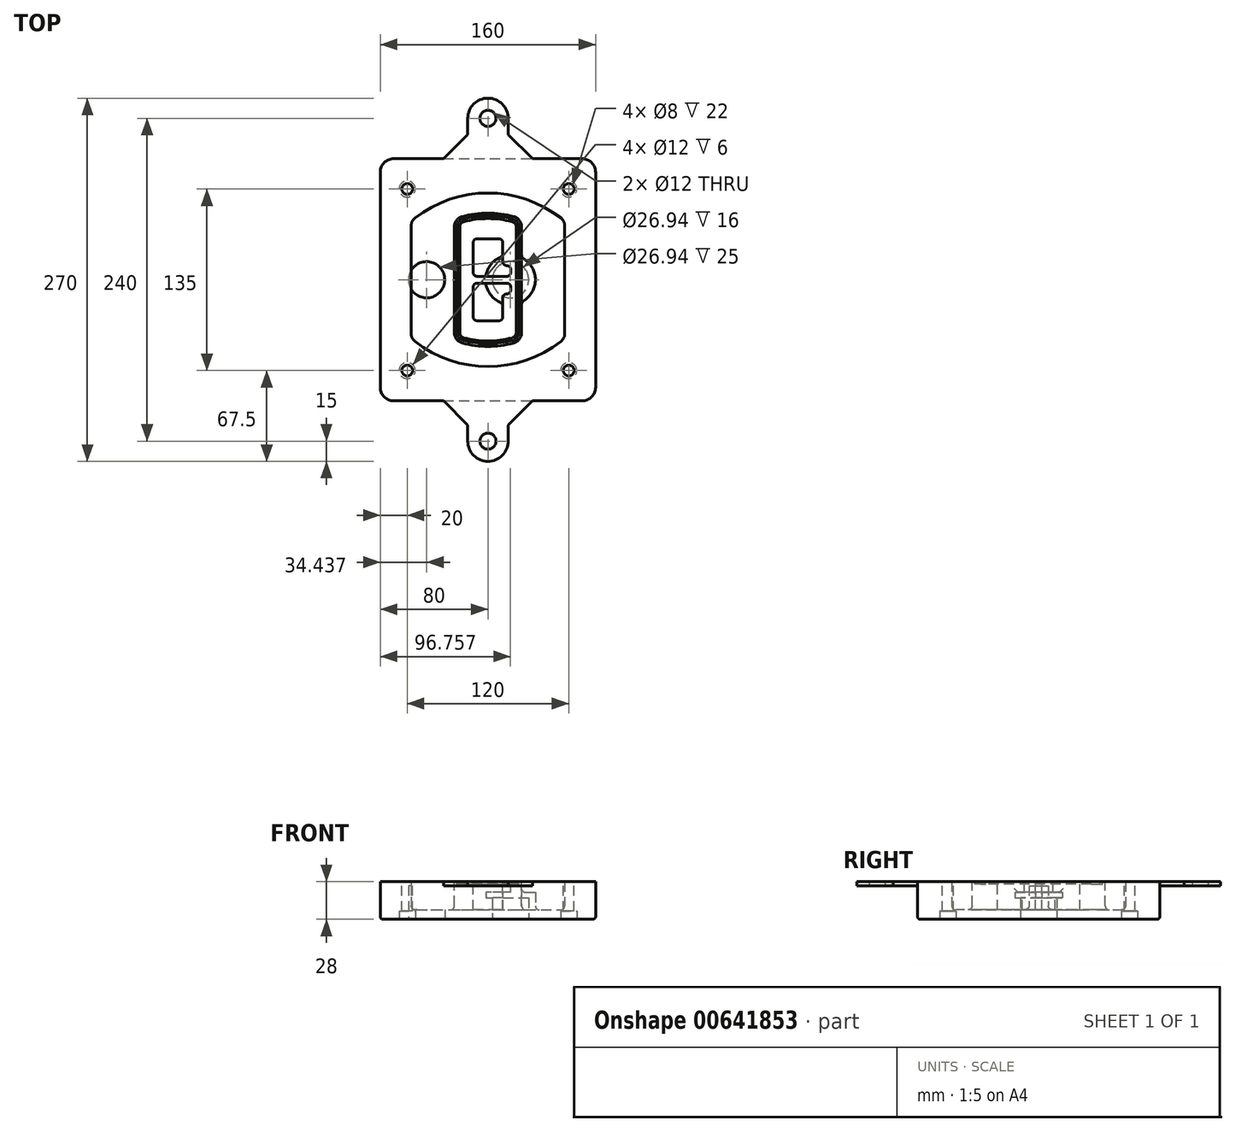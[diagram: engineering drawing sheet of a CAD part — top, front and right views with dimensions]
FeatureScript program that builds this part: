
annotation { "Feature Type Name" : "Feature", "Feature Type Description" : "" }
export const myFeature = defineFeature(function(context is Context, id is Id, definition is map)
    precondition{}
    {
        {
            var Q0;
            Q0=qCreatedBy(makeId("Top.planeOp"),FACE);
            var sketch = newSketch(context, id + "F0", { "sketchPlane" : qUnion([Q0])});
            skPoint(sketch, "E0.rect.middle", {"position": v(0, 0) * mm});
            skLineSegment(sketch, "E1.bottom", {"start": v(-70, -90) * mm, "end": v(70, -90) * mm});
            skLineSegment(sketch, "E1.top", {"start": v(-70, 90) * mm, "end": v(70, 90) * mm});
            skLineSegment(sketch, "E1.left", {"start": v(-80, -80) * mm, "end": v(-80, 80) * mm});
            skLineSegment(sketch, "E1.right", {"start": v(80, -80) * mm, "end": v(80, 80) * mm});
            skLineSegment(sketch, "E2", {"start": v(-80, 90) * mm, "end": v(80, -90) * mm, "construction": true});
            skLineSegment(sketch, "E3", {"start": v(80, 90) * mm, "end": v(-80, -90) * mm, "construction": true});
            skCircle(sketch, "E4", {"center": v(-60, 67.5) * mm, "radius": 4 * mm});
            skCircle(sketch, "E5", {"center": v(60, 67.5) * mm, "radius": 4 * mm});
            skCircle(sketch, "E6", {"center": v(60, -67.5) * mm, "radius": 4 * mm});
            skCircle(sketch, "E7", {"center": v(-60, -67.5) * mm, "radius": 4 * mm});
            skLineSegment(sketch, "E8", {"start": v(-60, 67.5) * mm, "end": v(60, 67.5) * mm, "construction": true});
            skLineSegment(sketch, "E9", {"start": v(60, 67.5) * mm, "end": v(60, -67.5) * mm, "construction": true});
            skLineSegment(sketch, "E10", {"start": v(60, -67.5) * mm, "end": v(-60, -67.5) * mm, "construction": true});
            skLineSegment(sketch, "E11", {"start": v(-60, -67.5) * mm, "end": v(-60, 67.5) * mm, "construction": true});
            skLineSegment(sketch, "E12", {"start": v(-60, 40.3) * mm, "end": v(-60, -40.3) * mm});
            skLineSegment(sketch, "E13", {"start": v(60, 40.3) * mm, "end": v(60, -40.3) * mm});
            skArc(sketch, "E14", {"start": v(56.15, 48.18) * mm, "mid": v(0, 67.5) * mm, "end": v(-56.15, 48.18) * mm});
            skArc(sketch, "E15", {"start": v(-56.15, -48.18) * mm, "mid": v(0, -67.5) * mm, "end": v(56.15, -48.18) * mm});
            skLineSegment(sketch, "E16", {"start": v(-60, 0) * mm, "end": v(60, 0) * mm, "construction": true});
            skPoint(sketch, "E17.visualSharp", {"position": v(-60, -45) * mm});
            skArc(sketch, "E17.filletArc", {"start": v(-60, -40.3) * mm, "mid": v(-58.99, -44.68) * mm, "end": v(-56.15, -48.18) * mm});
            skPoint(sketch, "E18.visualSharp", {"position": v(-60, 45) * mm});
            skArc(sketch, "E18.filletArc", {"start": v(-56.15, 48.18) * mm, "mid": v(-58.99, 44.68) * mm, "end": v(-60, 40.3) * mm});
            skPoint(sketch, "E19.visualSharp", {"position": v(60, 45) * mm});
            skArc(sketch, "E19.filletArc", {"start": v(60, 40.3) * mm, "mid": v(58.99, 44.68) * mm, "end": v(56.15, 48.18) * mm});
            skPoint(sketch, "E20.visualSharp", {"position": v(60, -45) * mm});
            skArc(sketch, "E20.filletArc", {"start": v(56.15, -48.18) * mm, "mid": v(58.99, -44.68) * mm, "end": v(60, -40.3) * mm});
            skPoint(sketch, "E21.visualSharp", {"position": v(-80, 90) * mm});
            skArc(sketch, "E21.filletArc", {"start": v(-70, 90) * mm, "mid": v(-77.07, 87.07) * mm, "end": v(-80, 80) * mm});
            skPoint(sketch, "E22.visualSharp", {"position": v(80, 90) * mm});
            skArc(sketch, "E22.filletArc", {"start": v(80, 80) * mm, "mid": v(77.07, 87.07) * mm, "end": v(70, 90) * mm});
            skPoint(sketch, "E23.visualSharp", {"position": v(80, -90) * mm});
            skArc(sketch, "E23.filletArc", {"start": v(70, -90) * mm, "mid": v(77.07, -87.07) * mm, "end": v(80, -80) * mm});
            skPoint(sketch, "E24.visualSharp", {"position": v(-80, -90) * mm});
            skArc(sketch, "E24.filletArc", {"start": v(-80, -80) * mm, "mid": v(-77.07, -87.07) * mm, "end": v(-70, -90) * mm});
            skArc(sketch, "E25.0", {"start": v(57, 40.3) * mm, "mid": v(56.3, 43.36) * mm, "end": v(54.3, 45.81) * mm});
            skLineSegment(sketch, "E25.1", {"start": v(57, 40.3) * mm, "end": v(57, -40.3) * mm});
            skArc(sketch, "E25.2", {"start": v(54.3, -45.81) * mm, "mid": v(56.3, -43.36) * mm, "end": v(57, -40.3) * mm});
            skArc(sketch, "E25.3", {"start": v(-54.3, -45.81) * mm, "mid": v(0, -64.5) * mm, "end": v(54.3, -45.81) * mm});
            skArc(sketch, "E25.4", {"start": v(-57, -40.3) * mm, "mid": v(-56.3, -43.36) * mm, "end": v(-54.3, -45.81) * mm});
            skArc(sketch, "E25.5", {"start": v(54.3, 45.81) * mm, "mid": v(0, 64.5) * mm, "end": v(-54.3, 45.81) * mm});
            skLineSegment(sketch, "E25.6", {"start": v(-57, 40.3) * mm, "end": v(-57, -40.3) * mm});
            skArc(sketch, "E25.7", {"start": v(-54.3, 45.81) * mm, "mid": v(-56.3, 43.36) * mm, "end": v(-57, 40.3) * mm});
            skArc(sketch, "E26.0", {"start": v(-58.62, 51.33) * mm, "mid": v(-62.58, 46.43) * mm, "end": v(-64, 40.3) * mm});
            skArc(sketch, "E26.1", {"start": v(58.62, 51.33) * mm, "mid": v(0, 71.5) * mm, "end": v(-58.62, 51.33) * mm});
            skArc(sketch, "E26.2", {"start": v(64, 40.3) * mm, "mid": v(62.58, 46.43) * mm, "end": v(58.62, 51.33) * mm});
            skLineSegment(sketch, "E26.3", {"start": v(64, 40.3) * mm, "end": v(64, -40.3) * mm});
            skArc(sketch, "E26.4", {"start": v(58.62, -51.33) * mm, "mid": v(62.58, -46.43) * mm, "end": v(64, -40.3) * mm});
            skLineSegment(sketch, "E26.5", {"start": v(-64, 40.3) * mm, "end": v(-64, -40.3) * mm});
            skArc(sketch, "E26.6", {"start": v(-58.62, -51.33) * mm, "mid": v(0, -71.5) * mm, "end": v(58.62, -51.33) * mm});
            skArc(sketch, "E26.7", {"start": v(-64, -40.3) * mm, "mid": v(-62.58, -46.43) * mm, "end": v(-58.62, -51.33) * mm});
            skSolve(sketch);
        }
        {
            var Q0;
            Q0=makeQuery(id+"F0.imprint","IMPRINT",FACE,{"disambiguationData":[TD([[makeQuery(id+"F0.imprint","IMPRINT",EDGE,{"derivedFrom":sQuery(id+"F0.wireOp",EDGE,"E1.bottom")}),1.0]])]});
            var Q1;
            Q1=makeQuery(id+"F0.imprint","IMPRINT",FACE,{"disambiguationData":[TD([[makeQuery(id+"F0.imprint","IMPRINT",EDGE,{"derivedFrom":sQuery(id+"F0.wireOp",EDGE,"E12")}),1.0]])]});
            var Q2;
            Q2=makeQuery(id+"F0.imprint","IMPRINT",FACE,{"disambiguationData":[TD([[makeQuery(id+"F0.imprint","IMPRINT",EDGE,{"derivedFrom":sQuery(id+"F0.wireOp",EDGE,"E25.0")}),1.0]])]});
            var Q3;
            Q3=makeQuery(id+"F0.imprint","IMPRINT",FACE,{"disambiguationData":[TD([[makeQuery(id+"F0.imprint","IMPRINT",EDGE,{"derivedFrom":sQuery(id+"F0.wireOp",EDGE,"E12")}),-1.0]])]});
            extrude(context, id + "F1", {"entities" : qUnion([Q0, Q1, Q2, Q3]), "oppositeDirection" : true, "depth" : 25 * mm});
        }
        {
            var Q0;
            Q0=makeQuery(id+"F0.imprint","IMPRINT",FACE,{"disambiguationData":[TD([[makeQuery(id+"F0.imprint","IMPRINT",EDGE,{"derivedFrom":sQuery(id+"F0.wireOp",EDGE,"E12")}),1.0]])]});
            extrude(context, id + "F2", {"entities" : qUnion([Q0]), "operationType" : NewBodyOperationType.ADD, "depth" : 3 * mm});
        }
        {
            var Q0;
            Q0=makeQuery(id+"F0.imprint","IMPRINT",FACE,{"disambiguationData":[TD([[makeQuery(id+"F0.imprint","IMPRINT",EDGE,{"derivedFrom":sQuery(id+"F0.wireOp",EDGE,"E25.0")}),1.0]])]});
            extrude(context, id + "F3", {"entities" : qUnion([Q0]), "operationType" : NewBodyOperationType.REMOVE, "oppositeDirection" : true, "depth" : 18 * mm});
        }
        {
            var Q0;
            Q0=makeQuery(id+"F2.opExtrude","CAP_FACE",FACE,{"disambiguationData":[OSD([sQuery(id+"F0.wireOp",EDGE,"E12"),sQuery(id+"F0.wireOp",EDGE,"E13"),sQuery(id+"F0.wireOp",EDGE,"E14"),sQuery(id+"F0.wireOp",EDGE,"E15"),sQuery(id+"F0.wireOp",EDGE,"E17.filletArc"),sQuery(id+"F0.wireOp",EDGE,"E18.filletArc"),sQuery(id+"F0.wireOp",EDGE,"E19.filletArc"),sQuery(id+"F0.wireOp",EDGE,"E20.filletArc"),sQuery(id+"F0.wireOp",EDGE,"E25.0"),sQuery(id+"F0.wireOp",EDGE,"E25.1"),sQuery(id+"F0.wireOp",EDGE,"E25.2"),sQuery(id+"F0.wireOp",EDGE,"E25.3"),sQuery(id+"F0.wireOp",EDGE,"E25.4"),sQuery(id+"F0.wireOp",EDGE,"E25.5"),sQuery(id+"F0.wireOp",EDGE,"E25.6"),sQuery(id+"F0.wireOp",EDGE,"E25.7")])],"isStart":false});
            var sketch = newSketch(context, id + "F4", { "sketchPlane" : qUnion([Q0])});
            skArc(sketch, "E27.0", {"start": v(-19.08, -46.97) * mm, "mid": v(0, -49.5) * mm, "end": v(19.08, -46.97) * mm});
            skArc(sketch, "E28.0", {"start": v(19.08, 46.97) * mm, "mid": v(0, 49.5) * mm, "end": v(-19.08, 46.97) * mm});
            skLineSegment(sketch, "E29", {"start": v(-25, 39.25) * mm, "end": v(-25, -39.25) * mm});
            skLineSegment(sketch, "E30", {"start": v(25, 39.25) * mm, "end": v(25, -39.25) * mm});
            skLineSegment(sketch, "E31", {"start": v(-25, 45.1) * mm, "end": v(25, 45.1) * mm, "construction": true});
            skLineSegment(sketch, "E32", {"start": v(-25, -45.1) * mm, "end": v(25, -45.1) * mm, "construction": true});
            skPoint(sketch, "E33.visualSharp", {"position": v(-25, 45.1) * mm});
            skArc(sketch, "E33.filletArc", {"start": v(-19.08, 46.97) * mm, "mid": v(-23.35, 44.11) * mm, "end": v(-25, 39.25) * mm});
            skPoint(sketch, "E34.visualSharp", {"position": v(25, 45.1) * mm});
            skArc(sketch, "E34.filletArc", {"start": v(25, 39.25) * mm, "mid": v(23.35, 44.11) * mm, "end": v(19.08, 46.97) * mm});
            skPoint(sketch, "E35.visualSharp", {"position": v(25, -45.1) * mm});
            skArc(sketch, "E35.filletArc", {"start": v(19.08, -46.97) * mm, "mid": v(23.35, -44.11) * mm, "end": v(25, -39.25) * mm});
            skPoint(sketch, "E36.visualSharp", {"position": v(-25, -45.1) * mm});
            skArc(sketch, "E36.filletArc", {"start": v(-25, -39.25) * mm, "mid": v(-23.35, -44.11) * mm, "end": v(-19.08, -46.97) * mm});
            skArc(sketch, "E37.0", {"start": v(54.3, 45.81) * mm, "mid": v(0, 64.5) * mm, "end": v(-54.3, 45.81) * mm});
            skArc(sketch, "E37.1", {"start": v(-54.3, 45.81) * mm, "mid": v(-56.3, 43.36) * mm, "end": v(-57, 40.3) * mm});
            skLineSegment(sketch, "E37.2", {"start": v(-57, 40.3) * mm, "end": v(-57, -40.3) * mm});
            skArc(sketch, "E37.3", {"start": v(-57, -40.3) * mm, "mid": v(-56.3, -43.36) * mm, "end": v(-54.3, -45.81) * mm});
            skArc(sketch, "E37.4", {"start": v(-54.3, -45.81) * mm, "mid": v(0, -64.5) * mm, "end": v(54.3, -45.81) * mm});
            skArc(sketch, "E37.5", {"start": v(54.3, -45.81) * mm, "mid": v(56.3, -43.36) * mm, "end": v(57, -40.3) * mm});
            skLineSegment(sketch, "E37.6", {"start": v(57, 40.3) * mm, "end": v(57, -40.3) * mm});
            skArc(sketch, "E37.7", {"start": v(57, 40.3) * mm, "mid": v(56.3, 43.36) * mm, "end": v(54.3, 45.81) * mm});
            skLineSegment(sketch, "E38.0", {"start": v(23, 39.25) * mm, "end": v(23, -39.25) * mm});
            skArc(sketch, "E38.1", {"start": v(18.56, -45.04) * mm, "mid": v(21.76, -42.9) * mm, "end": v(23, -39.25) * mm});
            skArc(sketch, "E38.2", {"start": v(-18.56, -45.04) * mm, "mid": v(0, -47.5) * mm, "end": v(18.56, -45.04) * mm});
            skArc(sketch, "E38.3", {"start": v(-23, -39.25) * mm, "mid": v(-21.76, -42.9) * mm, "end": v(-18.56, -45.04) * mm});
            skLineSegment(sketch, "E38.4", {"start": v(-23, 39.25) * mm, "end": v(-23, -39.25) * mm});
            skArc(sketch, "E38.5", {"start": v(23, 39.25) * mm, "mid": v(21.76, 42.9) * mm, "end": v(18.56, 45.04) * mm});
            skArc(sketch, "E38.6", {"start": v(-18.56, 45.04) * mm, "mid": v(-21.76, 42.9) * mm, "end": v(-23, 39.25) * mm});
            skArc(sketch, "E38.7", {"start": v(18.56, 45.04) * mm, "mid": v(0, 47.5) * mm, "end": v(-18.56, 45.04) * mm});
            skArc(sketch, "E39.0", {"start": v(21, 39.25) * mm, "mid": v(20.18, 41.68) * mm, "end": v(18.04, 43.1) * mm});
            skLineSegment(sketch, "E39.1", {"start": v(21, 39.25) * mm, "end": v(21, -39.25) * mm});
            skArc(sketch, "E39.2", {"start": v(18.04, -43.1) * mm, "mid": v(20.18, -41.68) * mm, "end": v(21, -39.25) * mm});
            skArc(sketch, "E39.3", {"start": v(-18.04, -43.1) * mm, "mid": v(0, -45.5) * mm, "end": v(18.04, -43.1) * mm});
            skArc(sketch, "E39.4", {"start": v(-21, -39.25) * mm, "mid": v(-20.18, -41.68) * mm, "end": v(-18.04, -43.1) * mm});
            skArc(sketch, "E39.5", {"start": v(18.04, 43.1) * mm, "mid": v(0, 45.5) * mm, "end": v(-18.04, 43.1) * mm});
            skLineSegment(sketch, "E39.6", {"start": v(-21, 39.25) * mm, "end": v(-21, -39.25) * mm});
            skArc(sketch, "E39.7", {"start": v(-18.04, 43.1) * mm, "mid": v(-20.18, 41.68) * mm, "end": v(-21, 39.25) * mm});
            skLineSegment(sketch, "E40", {"start": v(-25, 0) * mm, "end": v(25, 0) * mm, "construction": true});
            skLineSegment(sketch, "E41", {"start": v(-11, 5.5) * mm, "end": v(-11, 27.5) * mm});
            skLineSegment(sketch, "E42", {"start": v(-8, 30.5) * mm, "end": v(8, 30.5) * mm});
            skLineSegment(sketch, "E43", {"start": v(11, 27.5) * mm, "end": v(11, 13.5) * mm});
            skLineSegment(sketch, "E44", {"start": v(14, 10.5) * mm, "end": v(14, 10.5) * mm});
            skLineSegment(sketch, "E45", {"start": v(17, 7.5) * mm, "end": v(17, 5.5) * mm});
            skLineSegment(sketch, "E46", {"start": v(14, 2.5) * mm, "end": v(-8, 2.5) * mm});
            skPoint(sketch, "E47.visualSharp", {"position": v(-11, 30.5) * mm});
            skArc(sketch, "E47.filletArc", {"start": v(-8, 30.5) * mm, "mid": v(-10.12, 29.62) * mm, "end": v(-11, 27.5) * mm});
            skPoint(sketch, "E48.visualSharp", {"position": v(11, 30.5) * mm});
            skArc(sketch, "E48.filletArc", {"start": v(11, 27.5) * mm, "mid": v(10.12, 29.62) * mm, "end": v(8, 30.5) * mm});
            skPoint(sketch, "E49.visualSharp", {"position": v(11, 10.5) * mm});
            skArc(sketch, "E49.filletArc", {"start": v(11, 13.5) * mm, "mid": v(11.88, 11.38) * mm, "end": v(14, 10.5) * mm});
            skPoint(sketch, "E50.visualSharp", {"position": v(17, 10.5) * mm});
            skArc(sketch, "E50.filletArc", {"start": v(17, 7.5) * mm, "mid": v(16.12, 9.62) * mm, "end": v(14, 10.5) * mm});
            skPoint(sketch, "E51.visualSharp", {"position": v(17, 2.5) * mm});
            skArc(sketch, "E51.filletArc", {"start": v(14, 2.5) * mm, "mid": v(16.12, 3.38) * mm, "end": v(17, 5.5) * mm});
            skPoint(sketch, "E52.visualSharp", {"position": v(-11, 2.5) * mm});
            skArc(sketch, "E52.filletArc", {"start": v(-11, 5.5) * mm, "mid": v(-10.12, 3.38) * mm, "end": v(-8, 2.5) * mm});
            skLineSegment(sketch, "E53.0.MirrorCS", {"start": v(14, -2.5) * mm, "end": v(-8, -2.5) * mm});
            skArc(sketch, "E54.0.MirrorCS", {"start": v(-11, -5.5) * mm, "mid": v(-10.12, -3.38) * mm, "end": v(-8, -2.5) * mm});
            skLineSegment(sketch, "E55.0.MirrorCS", {"start": v(-11, -5.5) * mm, "end": v(-11, -27.5) * mm});
            skArc(sketch, "E56.0.MirrorCS", {"start": v(-8, -30.5) * mm, "mid": v(-10.12, -29.62) * mm, "end": v(-11, -27.5) * mm});
            skLineSegment(sketch, "E57.0.MirrorCS", {"start": v(-8, -30.5) * mm, "end": v(8, -30.5) * mm});
            skArc(sketch, "E58.0.MirrorCS", {"start": v(11, -27.5) * mm, "mid": v(10.12, -29.62) * mm, "end": v(8, -30.5) * mm});
            skLineSegment(sketch, "E59.0.MirrorCS", {"start": v(11, -27.5) * mm, "end": v(11, -13.5) * mm});
            skArc(sketch, "E60.0.MirrorCS", {"start": v(11, -13.5) * mm, "mid": v(11.88, -11.38) * mm, "end": v(14, -10.5) * mm});
            skArc(sketch, "E61.0.MirrorCS", {"start": v(17, -7.5) * mm, "mid": v(16.12, -9.62) * mm, "end": v(14, -10.5) * mm});
            skLineSegment(sketch, "E62.0.MirrorCS", {"start": v(17, -7.5) * mm, "end": v(17, -5.5) * mm});
            skArc(sketch, "E63.0.MirrorCS", {"start": v(14, -2.5) * mm, "mid": v(16.12, -3.38) * mm, "end": v(17, -5.5) * mm});
            skSolve(sketch);
        }
        {
            var Q0;
            Q0=makeQuery(id+"F4.imprint","IMPRINT",FACE,{"disambiguationData":[TD([[makeQuery(id+"F4.imprint","IMPRINT",EDGE,{"derivedFrom":sQuery(id+"F4.wireOp",EDGE,"E27.0")}),1.0]])]});
            var Q1;
            Q1=makeQuery(id+"F4.imprint","IMPRINT",FACE,{"disambiguationData":[TD([[makeQuery(id+"F4.imprint","IMPRINT",EDGE,{"derivedFrom":sQuery(id+"F4.wireOp",EDGE,"E38.0")}),-1.0]])]});
            var Q2;
            Q2=makeQuery(id+"F4.imprint","IMPRINT",FACE,{"disambiguationData":[TD([[makeQuery(id+"F4.imprint","IMPRINT",EDGE,{"derivedFrom":sQuery(id+"F4.wireOp",EDGE,"E39.0")}),1.0]])]});
            extrude(context, id + "F5", {"entities" : qUnion([Q0, Q1, Q2]), "operationType" : NewBodyOperationType.ADD, "endBound" : BoundingType.UP_TO_NEXT, "oppositeDirection" : true, "depth" : 25 * mm});
        }
        {
            var Q0;
            Q0=makeQuery(id+"F4.imprint","IMPRINT",FACE,{"disambiguationData":[TD([[makeQuery(id+"F4.imprint","IMPRINT",EDGE,{"derivedFrom":sQuery(id+"F4.wireOp",EDGE,"E38.0")}),-1.0]])]});
            extrude(context, id + "F6", {"entities" : qUnion([Q0]), "operationType" : NewBodyOperationType.REMOVE, "oppositeDirection" : true, "depth" : 2 * mm});
        }
        {
            var Q0;
            Q0=makeQuery(id+"F1.opExtrude","CAP_FACE",FACE,{"disambiguationData":[OSD([sQuery(id+"F0.wireOp",EDGE,"E1.bottom"),sQuery(id+"F0.wireOp",EDGE,"E1.top"),sQuery(id+"F0.wireOp",EDGE,"E1.left"),sQuery(id+"F0.wireOp",EDGE,"E1.right"),sQuery(id+"F0.wireOp",EDGE,"E4"),sQuery(id+"F0.wireOp",EDGE,"E5"),sQuery(id+"F0.wireOp",EDGE,"E6"),sQuery(id+"F0.wireOp",EDGE,"E7"),sQuery(id+"F0.wireOp",EDGE,"E21.filletArc"),sQuery(id+"F0.wireOp",EDGE,"E22.filletArc"),sQuery(id+"F0.wireOp",EDGE,"E23.filletArc"),sQuery(id+"F0.wireOp",EDGE,"E24.filletArc")])],"isStart":false});
            var sketch = newSketch(context, id + "F7", { "sketchPlane" : qUnion([Q0])});
            skCircle(sketch, "E64", {"center": v(16.76, 0) * mm, "radius": 13.47 * mm});
            skCircle(sketch, "E65", {"center": v(-45.56, 0) * mm, "radius": 13.47 * mm});
            skLineSegment(sketch, "E66", {"start": v(80, 0) * mm, "end": v(-80, 0) * mm});
            skCircle(sketch, "E67", {"center": v(16.76, 0) * mm, "radius": 18.47 * mm});
            skCircle(sketch, "E68", {"center": v(60, -67.5) * mm, "radius": 6 * mm});
            skCircle(sketch, "E69", {"center": v(-60, -67.5) * mm, "radius": 6 * mm});
            skCircle(sketch, "E70", {"center": v(-60, 67.5) * mm, "radius": 6 * mm});
            skCircle(sketch, "E71", {"center": v(60, 67.5) * mm, "radius": 6 * mm});
            skSolve(sketch);
        }
        {
            var Q0;
            {var subQ1=sQuery(id+"F7.wireOp",EDGE,"E66");var subQ4=sQuery(id+"F7.wireOp",EDGE,"E64");var subQ6=makeQuery(id+"F7.imprint","INTERSECT",VERTEX,{"disambiguationData":[OD(0.0)],"derivedFrom":[subQ4,subQ1]});Q0=makeQuery(id+"F7.imprint","IMPRINT",FACE,{"disambiguationData":[TD([[makeQuery(id+"F7.imprint","IMPRINT",EDGE,{"disambiguationData":[TD([[subQ6,-1.0]])],"derivedFrom":subQ4}),-1.0]])]});}
            var Q1;
            {var subQ0=sQuery(id+"F7.wireOp",EDGE,"E66");var subQ1=sQuery(id+"F7.wireOp",EDGE,"E64");var subQ3=makeQuery(id+"F7.imprint","INTERSECT",VERTEX,{"disambiguationData":[OD(0.0)],"derivedFrom":[subQ1,subQ0]});Q1=makeQuery(id+"F7.imprint","IMPRINT",FACE,{"disambiguationData":[TD([[makeQuery(id+"F7.imprint","IMPRINT",EDGE,{"disambiguationData":[TD([[subQ3,-1.0]])],"derivedFrom":subQ1}),1.0]])]});}
            var Q2;
            {var subQ0=sQuery(id+"F7.wireOp",EDGE,"E66");var subQ1=sQuery(id+"F7.wireOp",EDGE,"E64");var subQ3=makeQuery(id+"F7.imprint","INTERSECT",VERTEX,{"disambiguationData":[OD(0.0)],"derivedFrom":[subQ1,subQ0]});Q2=makeQuery(id+"F7.imprint","IMPRINT",FACE,{"disambiguationData":[TD([[makeQuery(id+"F7.imprint","IMPRINT",EDGE,{"disambiguationData":[TD([[subQ3,1.0]])],"derivedFrom":subQ1}),1.0]])]});}
            var Q3;
            {var subQ1=sQuery(id+"F7.wireOp",EDGE,"E66");var subQ4=sQuery(id+"F7.wireOp",EDGE,"E64");var subQ6=makeQuery(id+"F7.imprint","INTERSECT",VERTEX,{"disambiguationData":[OD(0.0)],"derivedFrom":[subQ4,subQ1]});Q3=makeQuery(id+"F7.imprint","IMPRINT",FACE,{"disambiguationData":[TD([[makeQuery(id+"F7.imprint","IMPRINT",EDGE,{"disambiguationData":[TD([[subQ6,1.0]])],"derivedFrom":subQ4}),-1.0]])]});}
            extrude(context, id + "F8", {"entities" : qUnion([Q0, Q1, Q2, Q3]), "operationType" : NewBodyOperationType.ADD, "oppositeDirection" : true, "depth" : 20 * mm});
        }
        {
            var Q0;
            {var subQ0=sQuery(id+"F7.wireOp",EDGE,"E66");var subQ1=sQuery(id+"F7.wireOp",EDGE,"E64");var subQ3=makeQuery(id+"F7.imprint","INTERSECT",VERTEX,{"disambiguationData":[OD(0.0)],"derivedFrom":[subQ1,subQ0]});Q0=makeQuery(id+"F7.imprint","IMPRINT",FACE,{"disambiguationData":[TD([[makeQuery(id+"F7.imprint","IMPRINT",EDGE,{"disambiguationData":[TD([[subQ3,-1.0]])],"derivedFrom":subQ1}),1.0]])]});}
            var Q1;
            {var subQ0=sQuery(id+"F7.wireOp",EDGE,"E66");var subQ1=sQuery(id+"F7.wireOp",EDGE,"E64");var subQ3=makeQuery(id+"F7.imprint","INTERSECT",VERTEX,{"disambiguationData":[OD(0.0)],"derivedFrom":[subQ1,subQ0]});Q1=makeQuery(id+"F7.imprint","IMPRINT",FACE,{"disambiguationData":[TD([[makeQuery(id+"F7.imprint","IMPRINT",EDGE,{"disambiguationData":[TD([[subQ3,1.0]])],"derivedFrom":subQ1}),1.0]])]});}
            extrude(context, id + "F9", {"entities" : qUnion([Q0, Q1]), "operationType" : NewBodyOperationType.REMOVE, "oppositeDirection" : true, "depth" : 16 * mm});
        }
        {
            var Q0;
            {var subQ0=sQuery(id+"F7.wireOp",EDGE,"E66");var subQ1=sQuery(id+"F7.wireOp",EDGE,"E65");var subQ3=makeQuery(id+"F7.imprint","INTERSECT",VERTEX,{"disambiguationData":[OD(0.0)],"derivedFrom":[subQ1,subQ0]});Q0=makeQuery(id+"F7.imprint","IMPRINT",FACE,{"disambiguationData":[TD([[makeQuery(id+"F7.imprint","IMPRINT",EDGE,{"disambiguationData":[TD([[subQ3,-1.0]])],"derivedFrom":subQ1}),1.0]])]});}
            var Q1;
            {var subQ0=sQuery(id+"F7.wireOp",EDGE,"E66");var subQ1=sQuery(id+"F7.wireOp",EDGE,"E65");var subQ3=makeQuery(id+"F7.imprint","INTERSECT",VERTEX,{"disambiguationData":[OD(0.0)],"derivedFrom":[subQ1,subQ0]});Q1=makeQuery(id+"F7.imprint","IMPRINT",FACE,{"disambiguationData":[TD([[makeQuery(id+"F7.imprint","IMPRINT",EDGE,{"disambiguationData":[TD([[subQ3,1.0]])],"derivedFrom":subQ1}),1.0]])]});}
            extrude(context, id + "F10", {"entities" : qUnion([Q0, Q1]), "operationType" : NewBodyOperationType.REMOVE, "oppositeDirection" : true, "depth" : 25 * mm});
        }
        {
            var Q0;
            Q0=makeQuery(id+"F7.imprint","IMPRINT",FACE,{"disambiguationData":[TD([[makeQuery(id+"F7.imprint","IMPRINT",EDGE,{"derivedFrom":sQuery(id+"F7.wireOp",EDGE,"E68")}),1.0]])]});
            var Q1;
            Q1=makeQuery(id+"F7.imprint","IMPRINT",FACE,{"disambiguationData":[TD([[makeQuery(id+"F7.imprint","IMPRINT",EDGE,{"derivedFrom":makeQuery(id+"F1.opExtrude","CAP_EDGE",EDGE,{"disambiguationData":[OSD([sQuery(id+"F0.wireOp",EDGE,"E5")])],"isStart":false})}),-1.0]])]});
            var Q2;
            Q2=makeQuery(id+"F7.imprint","IMPRINT",FACE,{"disambiguationData":[TD([[makeQuery(id+"F7.imprint","IMPRINT",EDGE,{"derivedFrom":sQuery(id+"F7.wireOp",EDGE,"E69")}),1.0]])]});
            var Q3;
            Q3=makeQuery(id+"F7.imprint","IMPRINT",FACE,{"disambiguationData":[TD([[makeQuery(id+"F7.imprint","IMPRINT",EDGE,{"derivedFrom":makeQuery(id+"F1.opExtrude","CAP_EDGE",EDGE,{"disambiguationData":[OSD([sQuery(id+"F0.wireOp",EDGE,"E4")])],"isStart":false})}),-1.0]])]});
            var Q4;
            Q4=makeQuery(id+"F7.imprint","IMPRINT",FACE,{"disambiguationData":[TD([[makeQuery(id+"F7.imprint","IMPRINT",EDGE,{"derivedFrom":sQuery(id+"F7.wireOp",EDGE,"E70")}),1.0]])]});
            var Q5;
            Q5=makeQuery(id+"F7.imprint","IMPRINT",FACE,{"disambiguationData":[TD([[makeQuery(id+"F7.imprint","IMPRINT",EDGE,{"derivedFrom":makeQuery(id+"F1.opExtrude","CAP_EDGE",EDGE,{"disambiguationData":[OSD([sQuery(id+"F0.wireOp",EDGE,"E7")])],"isStart":false})}),-1.0]])]});
            var Q6;
            Q6=makeQuery(id+"F7.imprint","IMPRINT",FACE,{"disambiguationData":[TD([[makeQuery(id+"F7.imprint","IMPRINT",EDGE,{"derivedFrom":sQuery(id+"F7.wireOp",EDGE,"E71")}),1.0]])]});
            var Q7;
            Q7=makeQuery(id+"F7.imprint","IMPRINT",FACE,{"disambiguationData":[TD([[makeQuery(id+"F7.imprint","IMPRINT",EDGE,{"derivedFrom":makeQuery(id+"F1.opExtrude","CAP_EDGE",EDGE,{"disambiguationData":[OSD([sQuery(id+"F0.wireOp",EDGE,"E6")])],"isStart":false})}),-1.0]])]});
            extrude(context, id + "F11", {"entities" : qUnion([Q0, Q1, Q2, Q3, Q4, Q5, Q6, Q7]), "operationType" : NewBodyOperationType.REMOVE, "oppositeDirection" : true, "depth" : 6 * mm});
        }
        {
            var Q0;
            Q0=makeQuery(id+"F9.boolean.opBoolean","COPY",FACE,{"derivedFrom":makeQuery(id+"F9.opExtrude","CAP_FACE",FACE,{"disambiguationData":[OSD([sQuery(id+"F7.wireOp",EDGE,"E64")])],"isStart":false})});
            var sketch = newSketch(context, id + "F12", { "sketchPlane" : qUnion([Q0])});
            skArc(sketch, "E72.0", {"start": v(11, 17.55) * mm, "mid": v(2.57, 11.82) * mm, "end": v(-1.54, 2.5) * mm});
            skArc(sketch, "E72.1", {"start": v(-1.54, -2.5) * mm, "mid": v(2.57, -11.82) * mm, "end": v(11, -17.55) * mm});
            skLineSegment(sketch, "E73", {"start": v(-1.54, -2.5) * mm, "end": v(14, -2.5) * mm});
            skLineSegment(sketch, "E74.0", {"start": v(14, 2.5) * mm, "end": v(-1.54, 2.5) * mm});
            skArc(sketch, "E74.1", {"start": v(14, 2.5) * mm, "mid": v(16.12, 3.38) * mm, "end": v(17, 5.5) * mm});
            skLineSegment(sketch, "E74.2", {"start": v(17, 7.5) * mm, "end": v(17, 5.5) * mm});
            skArc(sketch, "E74.3", {"start": v(17, 7.5) * mm, "mid": v(16.12, 9.62) * mm, "end": v(14, 10.5) * mm});
            skArc(sketch, "E74.4", {"start": v(11, 13.5) * mm, "mid": v(11.88, 11.38) * mm, "end": v(14, 10.5) * mm});
            skLineSegment(sketch, "E74.5", {"start": v(11, 17.55) * mm, "end": v(11, 13.5) * mm});
            skLineSegment(sketch, "E74.7", {"start": v(14, -2.5) * mm, "end": v(-1.54, -2.5) * mm});
            skArc(sketch, "E74.8", {"start": v(14, -2.5) * mm, "mid": v(16.12, -3.38) * mm, "end": v(17, -5.5) * mm});
            skLineSegment(sketch, "E74.9", {"start": v(17, -7.5) * mm, "end": v(17, -5.5) * mm});
            skArc(sketch, "E74.10", {"start": v(17, -7.5) * mm, "mid": v(16.12, -9.62) * mm, "end": v(14, -10.5) * mm});
            skArc(sketch, "E74.11", {"start": v(11, -13.5) * mm, "mid": v(11.88, -11.38) * mm, "end": v(14, -10.5) * mm});
            skLineSegment(sketch, "E74.12", {"start": v(11, -17.55) * mm, "end": v(11, -13.5) * mm});
            skPoint(sketch, "E75.orphan", {"position": v(11, -27.5) * mm});
            skPoint(sketch, "E76.orphan", {"position": v(-8, -2.5) * mm});
            skPoint(sketch, "E77.orphan", {"position": v(-8, 2.5) * mm});
            skPoint(sketch, "E78.orphan", {"position": v(11, 27.5) * mm});
            skSolve(sketch);
        }
        {
            var Q0;
            {var subQ7=sQuery(id+"F12.wireOp",EDGE,"E72.0");var subQ14=sQuery(id+"F12.wireOp",EDGE,"E72.1");var subQ16=sQuery(id+"F12.wireOp",EDGE,"E74.1");var subQ18=sQuery(id+"F12.wireOp",EDGE,"E74.8");Q0=qUnion([makeQuery(id+"F12.imprint","IMPRINT",FACE,{"disambiguationData":[TD([[makeQuery(id+"F12.imprint","IMPRINT",EDGE,{"derivedFrom":subQ7}),1.0]])]}),makeQuery(id+"F12.imprint","IMPRINT",FACE,{"disambiguationData":[TD([[makeQuery(id+"F12.imprint","IMPRINT",EDGE,{"derivedFrom":subQ14}),1.0]])]}),makeQuery(id+"F12.imprint","IMPRINT",FACE,{"disambiguationData":[TD([[makeQuery(id+"F12.imprint","IMPRINT",EDGE,{"derivedFrom":subQ16}),1.0]])]}),makeQuery(id+"F12.imprint","IMPRINT",FACE,{"disambiguationData":[TD([[makeQuery(id+"F12.imprint","IMPRINT",EDGE,{"derivedFrom":subQ18}),-1.0]])]})]);}
            var Q1;
            Q1=makeQuery(id+"F5.boolean.opBoolean","SPLIT",FACE,{"disambiguationData":[TD([makeQuery(id+"F5.opExtrude","SWEPT_FACE",FACE,{"disambiguationData":[OSD([sQuery(id+"F4.wireOp",EDGE,"E41")])]})])],"derivedFrom":makeQuery(id+"F3.boolean.opBoolean","COPY",FACE,{"derivedFrom":makeQuery(id+"F3.opExtrude","CAP_FACE",FACE,{"disambiguationData":[OSD([sQuery(id+"F0.wireOp",EDGE,"E25.0"),sQuery(id+"F0.wireOp",EDGE,"E25.1"),sQuery(id+"F0.wireOp",EDGE,"E25.2"),sQuery(id+"F0.wireOp",EDGE,"E25.3"),sQuery(id+"F0.wireOp",EDGE,"E25.4"),sQuery(id+"F0.wireOp",EDGE,"E25.5"),sQuery(id+"F0.wireOp",EDGE,"E25.6"),sQuery(id+"F0.wireOp",EDGE,"E25.7")])],"isStart":false})})});
            extrude(context, id + "F13", {"entities" : qUnion([Q0]), "operationType" : NewBodyOperationType.REMOVE, "endBound" : BoundingType.UP_TO_SURFACE, "endBoundEntityFace" : qUnion([Q1]), "depth" : 25 * mm});
        }
        {
            var Q0;
            Q0=makeQuery(id+"F3.boolean.opBoolean","COPY",EDGE,{"derivedFrom":makeQuery(id+"F3.opExtrude","CAP_EDGE",EDGE,{"disambiguationData":[OSD([sQuery(id+"F0.wireOp",EDGE,"E25.6")])],"isStart":false})});
            var Q1;
            Q1=makeQuery(id+"F8.boolean.opBoolean","INTERSECT",EDGE,{"derivedFrom":[makeQuery(id+"F5.opExtrude","SWEPT_FACE",FACE,{"disambiguationData":[OSD([sQuery(id+"F4.wireOp",EDGE,"E30")])]}),makeQuery(id+"F8.opExtrude","CAP_FACE",FACE,{"disambiguationData":[OSD([sQuery(id+"F7.wireOp",EDGE,"E67")])],"isStart":false})]});
            var Q2;
            Q2=makeQuery(id+"F8.boolean.opBoolean","INTERSECT",EDGE,{"disambiguationData":[OD(1.0)],"derivedFrom":[makeQuery(id+"F5.opExtrude","SWEPT_FACE",FACE,{"disambiguationData":[OSD([sQuery(id+"F4.wireOp",EDGE,"E30")])]}),makeQuery(id+"F8.opExtrude","SWEPT_FACE",FACE,{"disambiguationData":[OSD([sQuery(id+"F7.wireOp",EDGE,"E67")])]})]});
            var Q3;
            {var subQ0=sQuery(id+"F4.wireOp",EDGE,"E30");Q3=makeQuery(id+"F8.boolean.opBoolean","SPLIT",EDGE,{"disambiguationData":[TD([makeQuery(id+"F5.opExtrude","SWEPT_FACE",FACE,{"disambiguationData":[OSD([sQuery(id+"F4.wireOp",EDGE,"E35.filletArc")])]})])],"derivedFrom":makeQuery(id+"F5.opExtrude","CAP_EDGE",EDGE,{"disambiguationData":[OSD([subQ0])],"isStart":false})});}
            var Q4;
            {var subQ0=sQuery(id+"F0.wireOp",EDGE,"E25.7");var subQ1=sQuery(id+"F0.wireOp",EDGE,"E25.1");var subQ2=sQuery(id+"F0.wireOp",EDGE,"E25.6");var subQ3=sQuery(id+"F0.wireOp",EDGE,"E25.5");var subQ4=sQuery(id+"F0.wireOp",EDGE,"E25.4");var subQ5=sQuery(id+"F0.wireOp",EDGE,"E25.0");var subQ6=sQuery(id+"F0.wireOp",EDGE,"E25.2");var subQ7=sQuery(id+"F0.wireOp",EDGE,"E25.3");Q4=makeQuery(id+"F8.boolean.opBoolean","INTERSECT",EDGE,{"derivedFrom":[makeQuery(id+"F5.boolean.opBoolean","SPLIT",FACE,{"disambiguationData":[TD([makeQuery(id+"F2.opExtrude","SWEPT_FACE",FACE,{"disambiguationData":[OSD([subQ5])]})])],"derivedFrom":makeQuery(id+"F3.boolean.opBoolean","COPY",FACE,{"derivedFrom":makeQuery(id+"F3.opExtrude","CAP_FACE",FACE,{"disambiguationData":[OSD([subQ5,subQ1,subQ6,subQ7,subQ4,subQ3,subQ2,subQ0])],"isStart":false})})}),makeQuery(id+"F8.opExtrude","SWEPT_FACE",FACE,{"disambiguationData":[OSD([sQuery(id+"F7.wireOp",EDGE,"E67")])]})]});}
            var Q5;
            Q5=makeQuery(id+"F8.boolean.opBoolean","INTERSECT",EDGE,{"disambiguationData":[OD(0.0)],"derivedFrom":[makeQuery(id+"F5.opExtrude","SWEPT_FACE",FACE,{"disambiguationData":[OSD([sQuery(id+"F4.wireOp",EDGE,"E30")])]}),makeQuery(id+"F8.opExtrude","SWEPT_FACE",FACE,{"disambiguationData":[OSD([sQuery(id+"F7.wireOp",EDGE,"E67")])]})]});
            fillet(context, id + "F14", {"entities" : qUnion([Q0, Q1, Q2, Q3, Q4, Q5]), "radius" : 3 * mm, "tangentPropagation" : true, "allowEdgeOverflow" : false});
        }
        {
            var Q0;
            Q0=makeQuery(id+"F1.opExtrude","CAP_EDGE",EDGE,{"disambiguationData":[OSD([sQuery(id+"F0.wireOp",EDGE,"E1.bottom")])],"isStart":false});
            fillet(context, id + "F15", {"entities" : qUnion([Q0]), "radius" : 2 * mm, "tangentPropagation" : true, "allowEdgeOverflow" : false});
        }
        {
            var Q0;
            {var subQ0=sQuery(id+"F0.wireOp",EDGE,"E21.filletArc");var subQ1=sQuery(id+"F0.wireOp",EDGE,"E7");var subQ2=sQuery(id+"F0.wireOp",EDGE,"E6");var subQ3=sQuery(id+"F0.wireOp",EDGE,"E5");var subQ4=sQuery(id+"F0.wireOp",EDGE,"E4");var subQ5=sQuery(id+"F0.wireOp",EDGE,"E22.filletArc");var subQ6=sQuery(id+"F0.wireOp",EDGE,"E1.bottom");var subQ7=sQuery(id+"F0.wireOp",EDGE,"E1.right");var subQ8=sQuery(id+"F0.wireOp",EDGE,"E1.top");var subQ9=sQuery(id+"F0.wireOp",EDGE,"E1.left");var subQ10=sQuery(id+"F0.wireOp",EDGE,"E23.filletArc");var subQ11=sQuery(id+"F0.wireOp",EDGE,"E24.filletArc");Q0=makeQuery(id+"F2.boolean.opBoolean","SPLIT",FACE,{"disambiguationData":[TD([makeQuery(id+"F1.opExtrude","SWEPT_FACE",FACE,{"disambiguationData":[OSD([subQ6])]})])],"derivedFrom":makeQuery(id+"F1.opExtrude","CAP_FACE",FACE,{"disambiguationData":[OSD([subQ6,subQ8,subQ9,subQ7,subQ4,subQ3,subQ2,subQ1,subQ0,subQ5,subQ10,subQ11])],"isStart":true})});}
            var sketch = newSketch(context, id + "F16", { "sketchPlane" : qUnion([Q0])});
            skCircle(sketch, "E79", {"center": v(0, 120) * mm, "radius": 6 * mm});
            skPoint(sketch, "E79.centerSnap0", {"position": v(0, 90) * mm});
            skArc(sketch, "E80", {"start": v(15, 120) * mm, "mid": v(0, 135) * mm, "end": v(-15, 120) * mm});
            skLineSegment(sketch, "E81", {"start": v(-15, 120) * mm, "end": v(-15, 108) * mm});
            skLineSegment(sketch, "E82", {"start": v(-15, 108) * mm, "end": v(-33, 90) * mm});
            skLineSegment(sketch, "E83", {"start": v(15, 108) * mm, "end": v(15, 120) * mm});
            skLineSegment(sketch, "E84", {"start": v(15, 108) * mm, "end": v(33, 90) * mm});
            skLineSegment(sketch, "E85", {"start": v(-101.55, 0) * mm, "end": v(110.2, 0) * mm, "construction": true});
            skPoint(sketch, "E85.startSnap0", {"position": v(-80, 0) * mm});
            skPoint(sketch, "E85.endSnap0", {"position": v(80, 0) * mm});
            skArc(sketch, "E86.MirrorCS", {"start": v(15, -120) * mm, "mid": v(0, -135) * mm, "end": v(-15, -120) * mm});
            skLineSegment(sketch, "E87.MirrorCS", {"start": v(-15, -120) * mm, "end": v(-15, -108) * mm});
            skLineSegment(sketch, "E88.MirrorCS", {"start": v(-15, -108) * mm, "end": v(-33, -90) * mm});
            skLineSegment(sketch, "E89.MirrorCS", {"start": v(15, -108) * mm, "end": v(15, -120) * mm});
            skCircle(sketch, "E90.MirrorC", {"center": v(0, -120) * mm, "radius": 6 * mm});
            skLineSegment(sketch, "E91.MirrorCS", {"start": v(15, -108) * mm, "end": v(33, -90) * mm});
            skSolve(sketch);
        }
        {
            var Q0;
            Q0=makeQuery(id+"F16.imprint","IMPRINT",FACE,{"disambiguationData":[TD([[makeQuery(id+"F16.imprint","IMPRINT",EDGE,{"derivedFrom":sQuery(id+"F16.wireOp",EDGE,"E79")}),-1.0]])]});
            var Q1;
            Q1=makeQuery(id+"F16.imprint","IMPRINT",FACE,{"disambiguationData":[TD([[makeQuery(id+"F16.imprint","IMPRINT",EDGE,{"derivedFrom":makeQuery(id+"F1.opExtrude","CAP_EDGE",EDGE,{"disambiguationData":[OSD([sQuery(id+"F0.wireOp",EDGE,"E1.left")])],"isStart":true})}),-1.0]])]});
            var Q2;
            Q2=makeQuery(id+"F16.imprint","IMPRINT",FACE,{"disambiguationData":[TD([[makeQuery(id+"F16.imprint","IMPRINT",EDGE,{"derivedFrom":sQuery(id+"F16.wireOp",EDGE,"E87.MirrorCS")}),-1.0]])]});
            var Q3;
            Q3=makeQuery(id+"F2.opExtrude","CAP_FACE",FACE,{"disambiguationData":[OSD([sQuery(id+"F0.wireOp",EDGE,"E12"),sQuery(id+"F0.wireOp",EDGE,"E13"),sQuery(id+"F0.wireOp",EDGE,"E14"),sQuery(id+"F0.wireOp",EDGE,"E15"),sQuery(id+"F0.wireOp",EDGE,"E17.filletArc"),sQuery(id+"F0.wireOp",EDGE,"E18.filletArc"),sQuery(id+"F0.wireOp",EDGE,"E19.filletArc"),sQuery(id+"F0.wireOp",EDGE,"E20.filletArc"),sQuery(id+"F0.wireOp",EDGE,"E25.0"),sQuery(id+"F0.wireOp",EDGE,"E25.1"),sQuery(id+"F0.wireOp",EDGE,"E25.2"),sQuery(id+"F0.wireOp",EDGE,"E25.3"),sQuery(id+"F0.wireOp",EDGE,"E25.4"),sQuery(id+"F0.wireOp",EDGE,"E25.5"),sQuery(id+"F0.wireOp",EDGE,"E25.6"),sQuery(id+"F0.wireOp",EDGE,"E25.7")])],"isStart":false});
            extrude(context, id + "F17", {"entities" : qUnion([Q0, Q1, Q2]), "operationType" : NewBodyOperationType.ADD, "endBound" : BoundingType.UP_TO_SURFACE, "depth" : 25 * mm, "endBoundEntityFace" : qUnion([Q3]), "offsetDistance" : 25 * mm});
        }
    });
